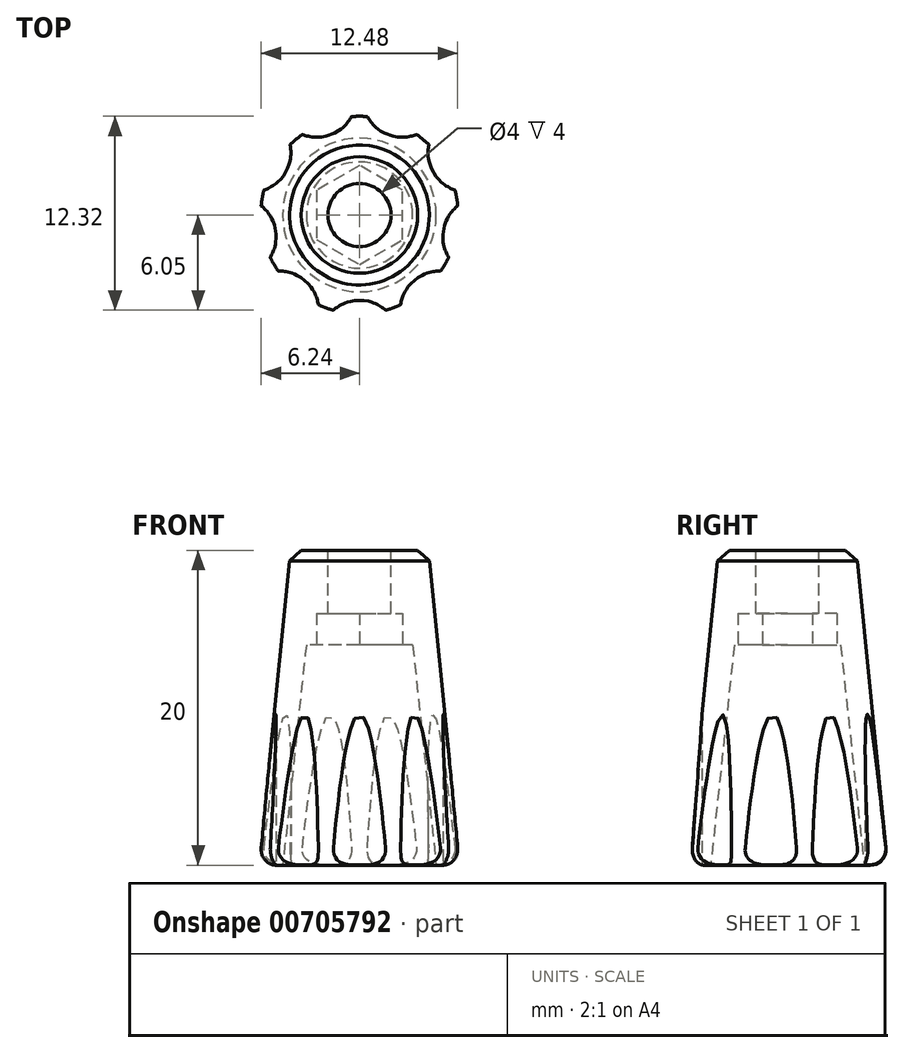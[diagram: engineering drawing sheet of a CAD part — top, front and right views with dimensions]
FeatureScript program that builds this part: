
annotation { "Feature Type Name" : "Feature", "Feature Type Description" : "" }
export const myFeature = defineFeature(function(context is Context, id is Id, definition is map)
    precondition{}
    {
        {
            var Q0;
            Q0=qCreatedBy(makeId("Top.planeOp"),FACE);
            var sketch = newSketch(context, id + "F0", { "sketchPlane" : qUnion([Q0])});
            skCircle(sketch, "E0", {"center": v(0, 0) * mm, "radius": 4.38 * mm});
            skSolve(sketch);
        }
        {
            var Q0;
            Q0=qCreatedBy(makeId("Top.planeOp"),FACE);
            cPlane(context, id + "F1", {"entities" : qUnion([Q0]), "cplaneType" : CPlaneType.OFFSET, "offset" : 20 * mm, "oppositeDirection" : true, "width" : 150 * mm, "height" : 150 * mm});
        }
        {
            var Q0;
            Q0=qCreatedBy(id+"F1.planeOp",FACE);
            var sketch = newSketch(context, id + "F2", { "sketchPlane" : qUnion([Q0])});
            skCircle(sketch, "E1", {"center": v(0, 0) * mm, "radius": 6.38 * mm});
            skSolve(sketch);
        }
        {
            var Q0;
            Q0=makeQuery(id+"F0.imprint","IMPRINT",FACE,{"disambiguationData":[TD([[makeQuery(id+"F0.imprint","IMPRINT",EDGE,{"derivedFrom":sQuery(id+"F0.wireOp",EDGE,"E0")}),1.0]])]});
            var Q1;
            Q1=makeQuery(id+"F2.imprint","IMPRINT",FACE,{"disambiguationData":[TD([[makeQuery(id+"F2.imprint","IMPRINT",EDGE,{"derivedFrom":sQuery(id+"F2.wireOp",EDGE,"E1")}),1.0]])]});
            loft(context, id + "F3", {"sheetProfilesArray" : [{ "sheetProfileEntities" : qUnion([Q0]) }, { "sheetProfileEntities" : qUnion([Q1]) }]});
        }
        {
            var Q0;
            Q0=makeQuery(id+"F3.opLoft","MID_CAP_EDGE",EDGE,{"disambiguationData":[OSD([sQuery(id+"F0.wireOp",EDGE,"E0")])],"capPos":0.0});
            chamfer(context, id + "F4", {"entities" : qUnion([Q0]), "width" : 0.75 * mm, "tangentPropagation" : true});
        }
        {
            var Q0;
            Q0=makeQuery(id+"F3.opLoft","CAP_FACE",FACE,{"disambiguationData":[OSD([makeQuery(id+"F0.imprint","IMPRINT",FACE,{"disambiguationData":[TD([[makeQuery(id+"F0.imprint","IMPRINT",EDGE,{"derivedFrom":sQuery(id+"F0.wireOp",EDGE,"E0")}),1.0]])]})])],"isStart":true});
            var sketch = newSketch(context, id + "F5", { "sketchPlane" : qUnion([Q0])});
            skCircle(sketch, "E2", {"center": v(0, 0) * mm, "radius": 2 * mm});
            skSolve(sketch);
        }
        {
            var Q0;
            Q0=qSketchRegion(id+"F5",true);
            extrude(context, id + "F6", {"entities" : qUnion([Q0]), "operationType" : NewBodyOperationType.REMOVE, "endBound" : BoundingType.THROUGH_ALL, "oppositeDirection" : true, "depth" : 25 * mm});
        }
        {
            var Q0;
            Q0=makeQuery(id+"F3.opLoft","CAP_FACE",FACE,{"disambiguationData":[OSD([makeQuery(id+"F0.imprint","IMPRINT",FACE,{"disambiguationData":[TD([[makeQuery(id+"F0.imprint","IMPRINT",EDGE,{"derivedFrom":sQuery(id+"F0.wireOp",EDGE,"E0")}),1.0]])]})])],"isStart":true});
            cPlane(context, id + "F7", {"entities" : qUnion([Q0]), "cplaneType" : CPlaneType.OFFSET, "offset" : 6 * mm, "oppositeDirection" : true, "width" : 150 * mm, "height" : 150 * mm});
        }
        {
            var Q0;
            Q0=qCreatedBy(id+"F7.planeOp",FACE);
            var sketch = newSketch(context, id + "F8", { "sketchPlane" : qUnion([Q0])});
            skCircle(sketch, "E3", {"center": v(0, 0) * mm, "radius": 3.38 * mm});
            skSolve(sketch);
        }
        {
            var Q0;
            Q0=makeQuery(id+"F3.opLoft","CAP_FACE",FACE,{"disambiguationData":[OSD([makeQuery(id+"F2.imprint","IMPRINT",FACE,{"disambiguationData":[TD([[makeQuery(id+"F2.imprint","IMPRINT",EDGE,{"derivedFrom":sQuery(id+"F2.wireOp",EDGE,"E1")}),1.0]])]})])],"isStart":true});
            var sketch = newSketch(context, id + "F9", { "sketchPlane" : qUnion([Q0])});
            skCircle(sketch, "E4", {"center": v(0, 0) * mm, "radius": 4.88 * mm});
            skSolve(sketch);
        }
        {
            var Q1;
            Q1=qSketchRegion(id+"F9",true);
            var Q2;
            Q2=qSketchRegion(id+"F8",true);
            loft(context, id + "F10", {"operationType" : NewBodyOperationType.REMOVE, "sheetProfilesArray" : [{ "sheetProfileEntities" : qUnion([Q1]) }, { "sheetProfileEntities" : qUnion([Q2]) }]});
        }
        {
            var Q0;
            Q0=makeQuery(id+"F10.boolean.opBoolean","COPY",FACE,{"derivedFrom":makeQuery(id+"F10.opLoft","CAP_FACE",FACE,{"disambiguationData":[OSD([makeQuery(id+"F8.imprint","IMPRINT",FACE,{"disambiguationData":[TD([[makeQuery(id+"F8.imprint","IMPRINT",EDGE,{"derivedFrom":sQuery(id+"F8.wireOp",EDGE,"E3")}),1.0]])]})])],"isStart":true})});
            var sketch = newSketch(context, id + "F11", { "sketchPlane" : qUnion([Q0])});
            skCircle(sketch, "E5.cCircle", {"center": v(0, 0) * mm, "radius": 2.73 * mm, "construction": true});
            skLineSegment(sketch, "E5.0", {"start": v(2.73, 1.57) * mm, "end": v(2.73, -1.57) * mm});
            skLineSegment(sketch, "E5.1", {"start": v(2.73, -1.57) * mm, "end": v(0, -3.15) * mm});
            skLineSegment(sketch, "E5.2", {"start": v(0, -3.15) * mm, "end": v(-2.73, -1.57) * mm});
            skLineSegment(sketch, "E5.3", {"start": v(-2.72, -1.57) * mm, "end": v(-2.73, 1.57) * mm});
            skLineSegment(sketch, "E5.4", {"start": v(-2.73, 1.57) * mm, "end": v(0, 3.15) * mm});
            skLineSegment(sketch, "E5.5", {"start": v(0, 3.15) * mm, "end": v(2.72, 1.57) * mm});
            skPoint(sketch, "E5.0.midPoint", {"position": v(2.73, 0) * mm});
            skSolve(sketch);
        }
        {
            var Q0;
            Q0=qSketchRegion(id+"F11",true);
            extrude(context, id + "F12", {"entities" : qUnion([Q0]), "operationType" : NewBodyOperationType.REMOVE, "oppositeDirection" : true, "depth" : (2) * mm});
        }
        {
            var Q0;
            Q0=makeQuery(id+"F3.opLoft","CAP_FACE",FACE,{"disambiguationData":[OSD([makeQuery(id+"F2.imprint","IMPRINT",FACE,{"disambiguationData":[TD([[makeQuery(id+"F2.imprint","IMPRINT",EDGE,{"derivedFrom":sQuery(id+"F2.wireOp",EDGE,"E1")}),1.0]])]})])],"isStart":true});
            var sketch = newSketch(context, id + "F13", { "sketchPlane" : qUnion([Q0])});
            skLineSegment(sketch, "E6", {"start": v(0, 0) * mm, "end": v(0, 6.38) * mm});
            skLineSegment(sketch, "E7", {"start": v(-1.75, 6.13) * mm, "end": v(1.75, 6.13) * mm});
            skArc(sketch, "E8", {"start": v(-1.75, 6.13) * mm, "mid": v(0, 5.42) * mm, "end": v(1.75, 6.13) * mm});
            skPoint(sketch, "E8.third.point", {"position": v(0, 5.42) * mm});
            skArc(sketch, "E9.1.0", {"start": v(-5.28, 3.57) * mm, "mid": v(-3.48, 4.15) * mm, "end": v(-2.6, 5.82) * mm});
            skArc(sketch, "E9.2.0", {"start": v(-6.34, -0.66) * mm, "mid": v(-5.33, 0.94) * mm, "end": v(-5.73, 2.79) * mm});
            skArc(sketch, "E9.3.0", {"start": v(-4.43, -4.58) * mm, "mid": v(-4.69, -2.7) * mm, "end": v(-6.18, -1.55) * mm});
            skArc(sketch, "E9.4.0", {"start": v(-0.45, -6.36) * mm, "mid": v(-1.85, -5.09) * mm, "end": v(-3.74, -5.16) * mm});
            skArc(sketch, "E9.5.0", {"start": v(3.74, -5.16) * mm, "mid": v(1.85, -5.09) * mm, "end": v(0.45, -6.36) * mm});
            skArc(sketch, "E9.6.0", {"start": v(6.18, -1.55) * mm, "mid": v(4.69, -2.7) * mm, "end": v(4.43, -4.58) * mm});
            skArc(sketch, "E9.7.0", {"start": v(5.73, 2.79) * mm, "mid": v(5.33, 0.94) * mm, "end": v(6.34, -0.66) * mm});
            skArc(sketch, "E9.8.0", {"start": v(2.6, 5.82) * mm, "mid": v(3.48, 4.15) * mm, "end": v(5.28, 3.57) * mm});
            skPoint(sketch, "E9.center", {"position": v(0, 0) * mm});
            skSolve(sketch);
        }
        {
            var Q0;
            Q0=qSketchRegion(id+"F13",true);
            var Q1;
            {var subQ0=sQuery(id+"F13.wireOp",EDGE,"E9.8.0");Q1=makeQuery(id+"F13.imprint","IMPRINT",FACE,{"disambiguationData":[TD([[makeQuery(id+"F13.imprint","IMPRINT",EDGE,{"derivedFrom":subQ0}),1.0]])]});}
            var Q2;
            {var subQ0=sQuery(id+"F13.wireOp",EDGE,"E9.7.0");Q2=makeQuery(id+"F13.imprint","IMPRINT",FACE,{"disambiguationData":[TD([[makeQuery(id+"F13.imprint","IMPRINT",EDGE,{"derivedFrom":subQ0}),1.0]])]});}
            var Q3;
            {var subQ0=sQuery(id+"F13.wireOp",EDGE,"E9.6.0");Q3=makeQuery(id+"F13.imprint","IMPRINT",FACE,{"disambiguationData":[TD([[makeQuery(id+"F13.imprint","IMPRINT",EDGE,{"derivedFrom":subQ0}),1.0]])]});}
            var Q4;
            {var subQ0=sQuery(id+"F13.wireOp",EDGE,"E9.5.0");Q4=makeQuery(id+"F13.imprint","IMPRINT",FACE,{"disambiguationData":[TD([[makeQuery(id+"F13.imprint","IMPRINT",EDGE,{"derivedFrom":subQ0}),1.0]])]});}
            var Q5;
            {var subQ0=sQuery(id+"F13.wireOp",EDGE,"E9.4.0");Q5=makeQuery(id+"F13.imprint","IMPRINT",FACE,{"disambiguationData":[TD([[makeQuery(id+"F13.imprint","IMPRINT",EDGE,{"derivedFrom":subQ0}),1.0]])]});}
            var Q6;
            {var subQ0=sQuery(id+"F13.wireOp",EDGE,"E9.3.0");Q6=makeQuery(id+"F13.imprint","IMPRINT",FACE,{"disambiguationData":[TD([[makeQuery(id+"F13.imprint","IMPRINT",EDGE,{"derivedFrom":subQ0}),1.0]])]});}
            var Q7;
            {var subQ0=sQuery(id+"F13.wireOp",EDGE,"E9.2.0");Q7=makeQuery(id+"F13.imprint","IMPRINT",FACE,{"disambiguationData":[TD([[makeQuery(id+"F13.imprint","IMPRINT",EDGE,{"derivedFrom":subQ0}),1.0]])]});}
            var Q8;
            {var subQ0=sQuery(id+"F13.wireOp",EDGE,"E9.1.0");Q8=makeQuery(id+"F13.imprint","IMPRINT",FACE,{"disambiguationData":[TD([[makeQuery(id+"F13.imprint","IMPRINT",EDGE,{"derivedFrom":subQ0}),1.0]])]});}
            var Q9;
            {var subQ0=sQuery(id+"F13.wireOp",EDGE,"E6");var subQ3=sQuery(id+"F13.wireOp",EDGE,"E7");var subQ4=makeQuery(id+"F13.imprint","INTERSECT",VERTEX,{"derivedFrom":[subQ0,subQ3]});Q9=makeQuery(id+"F13.imprint","IMPRINT",FACE,{"disambiguationData":[TD([[makeQuery(id+"F13.imprint","IMPRINT",EDGE,{"disambiguationData":[TD([[subQ4,-1.0]])],"derivedFrom":subQ0}),1.0]])]});}
            var Q10;
            {var subQ0=sQuery(id+"F13.wireOp",EDGE,"E6");var subQ3=sQuery(id+"F13.wireOp",EDGE,"E7");var subQ4=makeQuery(id+"F13.imprint","INTERSECT",VERTEX,{"derivedFrom":[subQ0,subQ3]});Q10=makeQuery(id+"F13.imprint","IMPRINT",FACE,{"disambiguationData":[TD([[makeQuery(id+"F13.imprint","IMPRINT",EDGE,{"disambiguationData":[TD([[subQ4,-1.0]])],"derivedFrom":subQ0}),-1.0]])]});}
            extrude(context, id + "F14", {"entities" : qUnion([Q0, Q1, Q2, Q3, Q4, Q5, Q6, Q7, Q8, Q9, Q10]), "operationType" : NewBodyOperationType.REMOVE, "oppositeDirection" : true, "depth" : 25 * mm});
        }
        {
            var Q0;
            {var subQ0=sQuery(id+"F2.wireOp",EDGE,"E1");var subQ1=sQuery(id+"F0.wireOp",EDGE,"E0");Q0=makeQuery(id+"F14.boolean.opBoolean","SPLIT",EDGE,{"disambiguationData":[TD([makeQuery(id+"F3.opLoft","SWEPT_FACE",FACE,{"disambiguationData":[OSD([subQ1,subQ0])]}),makeQuery(id+"F3.opLoft","CAP_FACE",FACE,{"disambiguationData":[OSD([makeQuery(id+"F2.imprint","IMPRINT",FACE,{"disambiguationData":[TD([[makeQuery(id+"F2.imprint","IMPRINT",EDGE,{"derivedFrom":subQ0}),1.0]])]})])],"isStart":true}),makeQuery(id+"F14.opExtrude","SWEPT_FACE",FACE,{"disambiguationData":[OSD([sQuery(id+"F13.wireOp",EDGE,"E9.1.0")])]}),makeQuery(id+"F14.opExtrude","SWEPT_FACE",FACE,{"disambiguationData":[OSD([sQuery(id+"F13.wireOp",EDGE,"E9.2.0")])]})])],"derivedFrom":makeQuery(id+"F3.opLoft","MID_CAP_EDGE",EDGE,{"disambiguationData":[OSD([subQ1,subQ0])],"capPos":1.0})});}
            fillet(context, id + "F15", {"entities" : qUnion([Q0]), "radius" : 1 * mm, "tangentPropagation" : true, "allowEdgeOverflow" : false});
        }
    });
